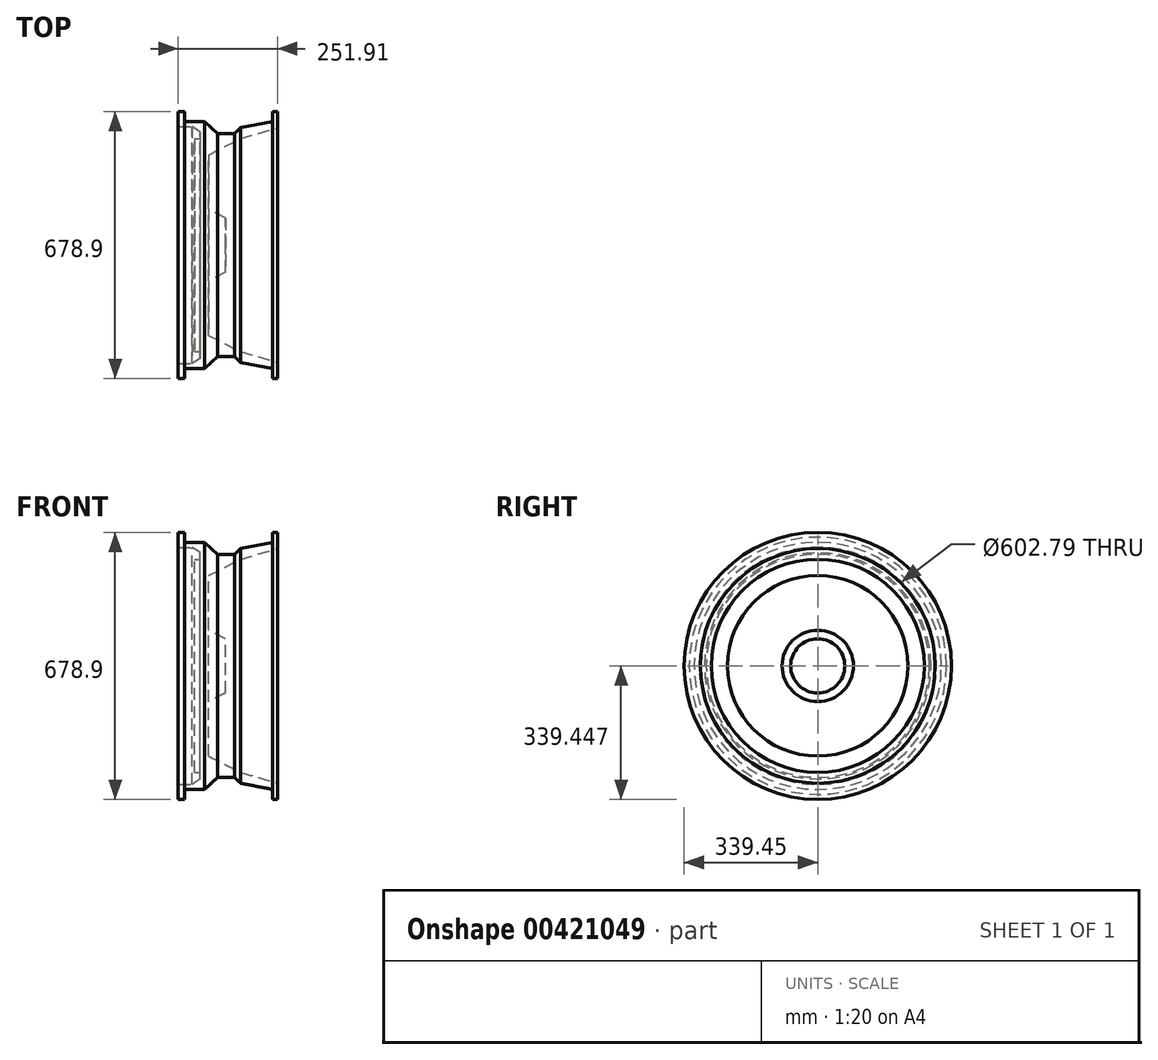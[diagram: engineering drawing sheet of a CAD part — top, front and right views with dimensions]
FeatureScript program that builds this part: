
annotation { "Feature Type Name" : "Feature", "Feature Type Description" : "" }
export const myFeature = defineFeature(function(context is Context, id is Id, definition is map)
    precondition{}
    {
        {
            var Q0;
            Q0=qCreatedBy(makeId("Front.planeOp"),FACE);
            var sketch = newSketch(context, id + "F0", { "sketchPlane" : qUnion([Q0])});
            skLineSegment(sketch, "E0", {"start": v(-76.66, 68.8) * mm, "end": v(-76.66, 56.1) * mm});
            skLineSegment(sketch, "E1", {"start": v(-76.66, 68.8) * mm, "end": v(-63.96, 68.8) * mm});
            skLineSegment(sketch, "E2", {"start": v(-63.96, 68.8) * mm, "end": v(-61.2, 68.8) * mm});
            skLineSegment(sketch, "E3", {"start": v(-61.2, 68.8) * mm, "end": v(-61.2, 43.4) * mm});
            skLineSegment(sketch, "E4", {"start": v(-61.2, 43.4) * mm, "end": v(-10.4, 43.4) * mm});
            skLineSegment(sketch, "E5", {"start": v(-10.4, 43.4) * mm, "end": v(23.58, 12.82) * mm});
            skLineSegment(sketch, "E6", {"start": v(23.58, 12.82) * mm, "end": v(66.27, 12.82) * mm});
            skLineSegment(sketch, "E7", {"start": v(66.27, 12.82) * mm, "end": v(81.74, 27.43) * mm});
            skLineSegment(sketch, "E8", {"start": v(81.74, 27.43) * mm, "end": v(162.55, 43.4) * mm});
            skLineSegment(sketch, "E9", {"start": v(162.55, 43.4) * mm, "end": v(162.55, 68.8) * mm});
            skLineSegment(sketch, "E10", {"start": v(162.55, 68.8) * mm, "end": v(175.25, 68.8) * mm});
            skLineSegment(sketch, "E11", {"start": v(175.25, 68.8) * mm, "end": v(175.25, 27.43) * mm});
            skLineSegment(sketch, "E12", {"start": v(175.25, 27.43) * mm, "end": v(81.74, 0) * mm});
            skLineSegment(sketch, "E13", {"start": v(81.74, 0) * mm, "end": v(0, -41.28) * mm});
            skLineSegment(sketch, "E14", {"start": v(-35.84, 0) * mm, "end": v(-21.94, 0) * mm});
            skLineSegment(sketch, "E15", {"start": v(-21.94, 0) * mm, "end": v(-21.94, 16.9) * mm});
            skLineSegment(sketch, "E16", {"start": v(-21.94, 16.9) * mm, "end": v(-41.53, 30.75) * mm});
            skLineSegment(sketch, "E17", {"start": v(-41.53, 30.75) * mm, "end": v(-75.8, 30.75) * mm});
            skLineSegment(sketch, "E18", {"start": v(-75.8, 30.75) * mm, "end": v(-76.66, 56.1) * mm});
            skLineSegment(sketch, "E19", {"start": v(0, -41.28) * mm, "end": v(0, -180.08) * mm});
            skLineSegment(sketch, "E20", {"start": v(0, -180.08) * mm, "end": v(42.96, -201.81) * mm});
            skLineSegment(sketch, "E21", {"start": v(42.96, -201.81) * mm, "end": v(42.96, -270.64) * mm});
            skLineSegment(sketch, "E22", {"start": v(42.96, -270.64) * mm, "end": v(-35.84, -270.64) * mm});
            skLineSegment(sketch, "E23", {"start": v(-35.84, -270.64) * mm, "end": v(-35.84, 0) * mm});
            skPoint(sketch, "E24.orphan", {"position": v(-39.57, 0) * mm});
            skSolve(sketch);
        }
        {
            var Q0;
            Q0=makeQuery(id+"F0.imprint","IMPRINT",FACE,{"disambiguationData":[TD([[makeQuery(id+"F0.imprint","IMPRINT",EDGE,{"derivedFrom":sQuery(id+"F0.wireOp",EDGE,"E0")}),1.0]])]});
            var Q1;
            Q1=sQuery(id+"F0.wireOp",EDGE,"E22");
            revolve(context, id + "F1", {"entities" : qUnion([Q0]), "axis" : qUnion([Q1]), "revolveType" : RevolveType.FULL});
        }
    });
